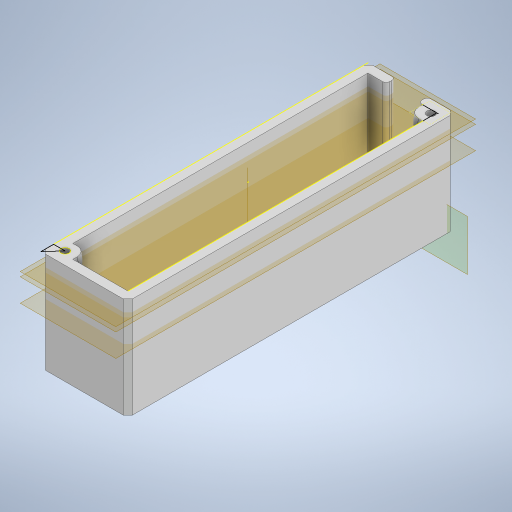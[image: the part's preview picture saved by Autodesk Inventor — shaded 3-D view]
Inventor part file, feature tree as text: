
AUTODESK INVENTOR PART (.ipt)
format: ipt  version: 2024 (Build 280153020, 153B)  size: 408,064 bytes
history: native  units: mm
features: sketch x10, extrude x6, plane x4, fillet x2, hole x1, loft x1, pattern_circular x1, chamfer x1, projected_geometry x1, other x1
ambient origin geometry x8: Origin, YZ Plane, XZ Plane, XY Plane, X Axis, Y Axis, Z Axis, Center Point
bodies: Solid1 (feature_tree)
feature tree (28):
  sketch  "Sketch1"  dims[d0=30.0mm d1=135.0mm]
  extrude  "Extrusion1"  Depth=135.0mm
  extrude  "Extrusion2"  Depth=44.0mm TaperAngle=0.0deg
  hole  "Hole1"  [1 undecoded]
  plane  "Work Plane1"
  extrude  "Extrusion3"  Depth=14.0mm
  sketch  "Sketch4"  dims[d11=80.0mm]
  extrude  "Extrusion4"  Depth=10.25mm TaperAngle=0.0deg
  plane  "Work Plane2"
  sketch  "Sketch6"  dims[d20=50.0mm d21=10.25mm d22=0.0mm]
  plane  "Work Plane3"
  sketch  "Sketch7"  dims[d31=21.0mm d32=0.0mm d33=-7.0mm d34=-10.0mm]
  sketch  "Sketch8"  dims[d35=8.0mm d36=8.0mm]
  loft  "Loft1"
  fillet  "Fillet2"  [1 undecoded]
  plane  "Work Plane4"
  sketch  "Sketch9"  dims[d39=9.0mm d40=9.0mm]
  extrude  "Extrusion5"  Depth=8.0mm
  extrude  "Extrusion6"  Depth=9.0mm
  pattern_circular  "Circular Pattern1"  Angle=90.0deg  [1 undecoded]
  fillet  "Fillet3"  [1 undecoded]
  sketch  "Sketch11"  dims[d41=0.0mm d42=90.0deg d43=0.0mm d44=90.0deg d45=0.0mm d46=90.0deg d47=4.25mm d48=-5.0mm d49=5.0mm d50=2.8194mm d51=3.5mm d52=2.75mm d53=0.0mm d54=13.0mm d55=0.0mm d56=20.0mm d57=180.0deg d59=1.5mm d60=2.0mm d61=2.0mm d62=45.0deg]
  chamfer  "Chamfer2"  Distance=4.25mm
  sketch  "Sketch2"  dims[d2=4.0mm d3=44.0mm d4=0.0mm]
  sketch  "Sketch3"  dims[d5=4.0mm d6=0.0mm d10=40.0mm]
  sketch  "Sketch5"  dims[d12=5.0mm d13=6.0mm d14=9.5mm d15=2.0mm d16=90.0deg d17=8.0mm d18=20.594885mm d19=14.0mm]
  projected_geometry  "Projected Loop1"
  other  "Work Axis1"
note: 4 required parameter values undecoded (feature->parameter linkage not recoverable at this tier; creation-order binding heuristic only, values carry confidence <= 0.55)
